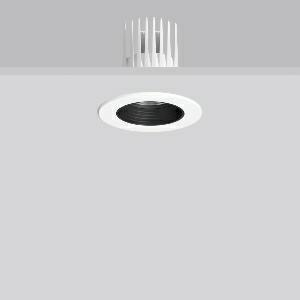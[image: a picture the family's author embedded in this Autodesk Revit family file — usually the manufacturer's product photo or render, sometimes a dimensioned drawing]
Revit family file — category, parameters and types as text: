
# Revit family: heledon_mini_e_901751_002_3_76_998f
name_source: partatom
category: Lighting Fixtures
units: mm (PartAtom-declared; Revit-internal decimal feet)

## family parameters
Cut with Voids When Loaded = No
Host = Face
Light Source = No
Part Type = Normal
Room Calculation Point = No
Round Connector Dimension = Use Diameter
Shared = No

## types (1)
- HELEDON mini E (1 x LED Modul 935, 3250 lm, 3500)
    Apparent Load = 29 VA
    Approval mark = CE
    CIE Flux Codes = 99 100 100 100 100
    Color Rendering = 92
    Color Temperature = 3500
    Default Elevation = 1800 mm
    Description = Series: HELEDON mini
Round recessed downlight. Housing: die-cast aluminium, powder-coated. Black plastic ring and recessed LED to prevent glare from the side. Optical assembly with lens made of plastic (polycarbonate) for the best homogeneous light distribution - can be changed without tools. Best colour rendering index Ra>90. Suitable for Recessed ceiling mounting. Installation without tools thanks to spring fastening system. Including separate LED converter with connecting cable 600 mm.High quality converter without flickering and stroboscopic effect. Through-wiring box (5 pole) available as accessory. The following accessories can be mounted without use of tools: interchangeable lenses, decorative glasses, honeycomb louvre, clear and frosted diffusers, white interchangeable plastic ring. 
Colour: traffic white, matt (RAL 9016)
Diameter: 124 mm
Height: 3 mm
Cut-out diameter: 114 mm
Recess height: 170 mm
Luminaire: recess height: 120 mm
Lamp: LED
Socket: without socket
Colour temperature: 3500K
Colour rendering index (CRI): 92
System power: 29 W
Rated luminous flux: 3250 lm
Luminous efficiency: 112 lm/W
Control gear: Converter, dimmable, DALI
Protection class: II
Type of protection: IP 20
    Height = 0 mm  [stored 0 ft]
    Lamp = 1 x LED Modul 935
    Lamp Light Flux = 3250 lm
    Lamp count = 1
    Length = 124 mm  [stored 0.406824 ft]
    Lifetime = 50000 h
    Luminous efficacy = 112 lm/W
    Manufacturer = RZB
    ModVariant = No
    Model = 901751.002.3.76
    Mounting Place = Ceiling
    Mounting Type = Recessed
    Number of Poles = 1
    OnlyDefault = Yes
    Power Factor = 1
    Product Name = HELEDON mini E
    Product group = Recessed downlights
    ProductGroupID = 402
    Protection Class = Protection class II
    Protection Degree = IP 20
    RLX_Detail_Level = 1
    RLX_Emergency_Light_Flux = 0 lm
    RLX_Emergency_Type = 0
    RLX_Emergency_Type_DB = No
    RlxData = <blob elided: 126029 chars, md5=78f618d2>
    Socket = socket
    Standby Power = 0 W
    System Light Flux = 3250 lm
    System Power = 29 W
    Type Comments = Product without accessories
    Type Image = 901656.002.jpg
    URL = http://relux.com
    VarID = ---
    Voltage = 230 V
    Voltage Range = 220-240 V
    Weight = 0.00 kg
    Width = 0 mm  [stored 0 ft]

note: [stored X ft] marks values corroborated as IEEE doubles in the binary element streams (Revit-internal decimal feet)

## geometry (parser evidence)
native form markers: Blend x4, Sweep x10
no freeform markers — native parametric forms only
